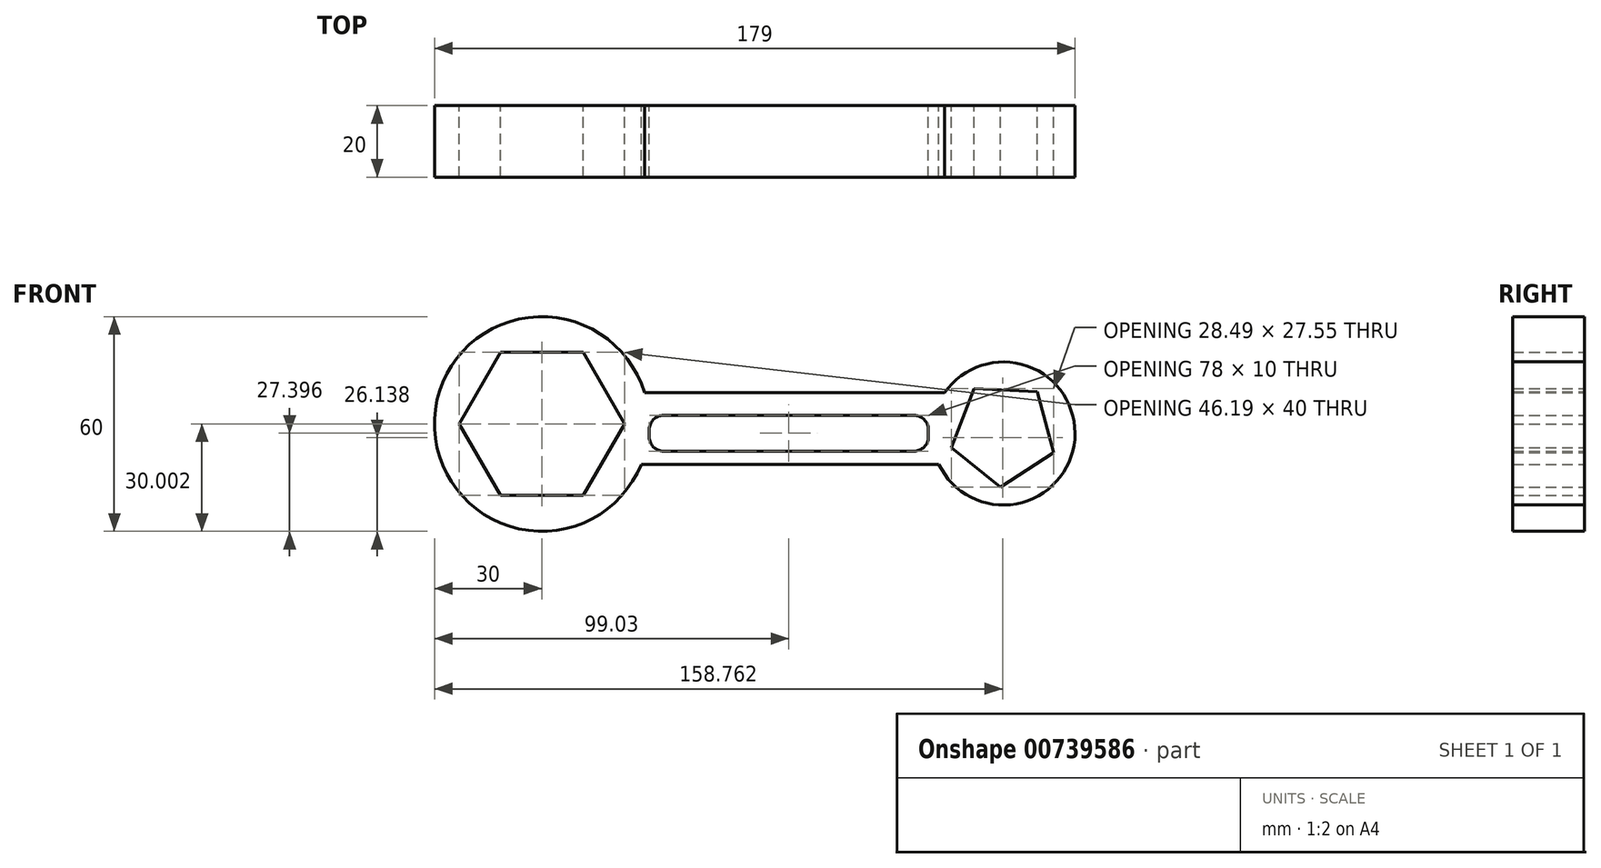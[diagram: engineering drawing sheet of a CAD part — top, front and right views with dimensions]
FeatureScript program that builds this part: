
annotation { "Feature Type Name" : "Feature", "Feature Type Description" : "" }
export const myFeature = defineFeature(function(context is Context, id is Id, definition is map)
    precondition{}
    {
        {
            var Q0;
            Q0=qCreatedBy(makeId("Front.planeOp"),FACE);
            var sketch = newSketch(context, id + "F0", { "sketchPlane" : qUnion([Q0])});
            skCircle(sketch, "E0", {"center": v(-69.03, 11.26) * mm, "radius": 30 * mm});
            skCircle(sketch, "E1", {"center": v(59.97, 8.6) * mm, "radius": 20 * mm});
            skLineSegment(sketch, "E2", {"start": v(-40.33, 20) * mm, "end": v(43.54, 20) * mm});
            skLineSegment(sketch, "E3", {"start": v(-41.22, 0) * mm, "end": v(41.91, 0) * mm});
            skCircle(sketch, "E4.cCircle", {"center": v(-69.03, 11.26) * mm, "radius": 20 * mm, "construction": true});
            skLineSegment(sketch, "E4.0", {"start": v(-80.58, 31.26) * mm, "end": v(-57.48, 31.26) * mm});
            skLineSegment(sketch, "E4.1", {"start": v(-57.48, 31.26) * mm, "end": v(-45.94, 11.26) * mm});
            skLineSegment(sketch, "E4.2", {"start": v(-45.94, 11.26) * mm, "end": v(-57.48, -8.74) * mm});
            skLineSegment(sketch, "E4.3", {"start": v(-57.48, -8.74) * mm, "end": v(-80.58, -8.74) * mm});
            skLineSegment(sketch, "E4.4", {"start": v(-80.58, -8.74) * mm, "end": v(-92.12, 11.26) * mm});
            skLineSegment(sketch, "E4.5", {"start": v(-92.12, 11.26) * mm, "end": v(-80.58, 31.26) * mm});
            skPoint(sketch, "E4.0.midPoint", {"position": v(-69.03, 31.26) * mm});
            skCircle(sketch, "E5.cCircle", {"center": v(59.97, 8.6) * mm, "radius": 12.14 * mm, "construction": true});
            skLineSegment(sketch, "E5.0", {"start": v(69.4, 20.27) * mm, "end": v(73.98, 3.24) * mm});
            skLineSegment(sketch, "E5.1", {"start": v(73.98, 3.24) * mm, "end": v(59.2, -6.38) * mm});
            skLineSegment(sketch, "E5.2", {"start": v(59.2, -6.38) * mm, "end": v(45.49, 4.7) * mm});
            skLineSegment(sketch, "E5.3", {"start": v(45.49, 4.7) * mm, "end": v(51.79, 21.17) * mm});
            skLineSegment(sketch, "E5.4", {"start": v(51.79, 21.17) * mm, "end": v(69.4, 20.27) * mm});
            skPoint(sketch, "E5.0.midPoint", {"position": v(71.69, 11.76) * mm});
            skLineSegment(sketch, "E6.bottom", {"start": v(-35, 13.66) * mm, "end": v(35, 13.66) * mm});
            skLineSegment(sketch, "E6.top", {"start": v(-35, 3.66) * mm, "end": v(35, 3.66) * mm});
            skLineSegment(sketch, "E6.left", {"start": v(-39, 9.66) * mm, "end": v(-39, 7.66) * mm});
            skLineSegment(sketch, "E6.right", {"start": v(39, 9.66) * mm, "end": v(39, 7.66) * mm});
            skPoint(sketch, "E6.middle", {"position": v(0, 8.66) * mm});
            skPoint(sketch, "E7.visualSharp", {"position": v(39, 3.66) * mm});
            skArc(sketch, "E7.filletArc", {"start": v(35, 3.66) * mm, "mid": v(37.83, 4.83) * mm, "end": v(39, 7.66) * mm});
            skPoint(sketch, "E8.visualSharp", {"position": v(39, 13.66) * mm});
            skArc(sketch, "E8.filletArc", {"start": v(39, 9.66) * mm, "mid": v(37.83, 12.48) * mm, "end": v(35, 13.66) * mm});
            skPoint(sketch, "E9.visualSharp", {"position": v(-39, 13.66) * mm});
            skArc(sketch, "E9.filletArc", {"start": v(-35, 13.66) * mm, "mid": v(-37.83, 12.48) * mm, "end": v(-39, 9.66) * mm});
            skPoint(sketch, "E10.visualSharp", {"position": v(-39, 3.66) * mm});
            skArc(sketch, "E10.filletArc", {"start": v(-39, 7.66) * mm, "mid": v(-37.83, 4.83) * mm, "end": v(-35, 3.66) * mm});
            skSolve(sketch);
        }
        {
            var Q0;
            Q0=makeQuery(id+"F0.imprint","IMPRINT",FACE,{"disambiguationData":[TD([[makeQuery(id+"F0.imprint","IMPRINT",EDGE,{"derivedFrom":sQuery(id+"F0.wireOp",EDGE,"E5.0")}),1.0]])]});
            var Q1;
            {var subQ0=sQuery(id+"F0.wireOp",EDGE,"E2");Q1=makeQuery(id+"F0.imprint","IMPRINT",FACE,{"disambiguationData":[TD([[makeQuery(id+"F0.imprint","IMPRINT",EDGE,{"derivedFrom":subQ0}),-1.0]])]});}
            var Q2;
            Q2=makeQuery(id+"F0.imprint","IMPRINT",FACE,{"disambiguationData":[TD([[makeQuery(id+"F0.imprint","IMPRINT",EDGE,{"derivedFrom":sQuery(id+"F0.wireOp",EDGE,"E4.0")}),1.0]])]});
            extrude(context, id + "F1", {"entities" : qUnion([Q0, Q1, Q2]), "depth" : 20 * mm, "offsetDistance" : 25 * mm});
        }
    });
